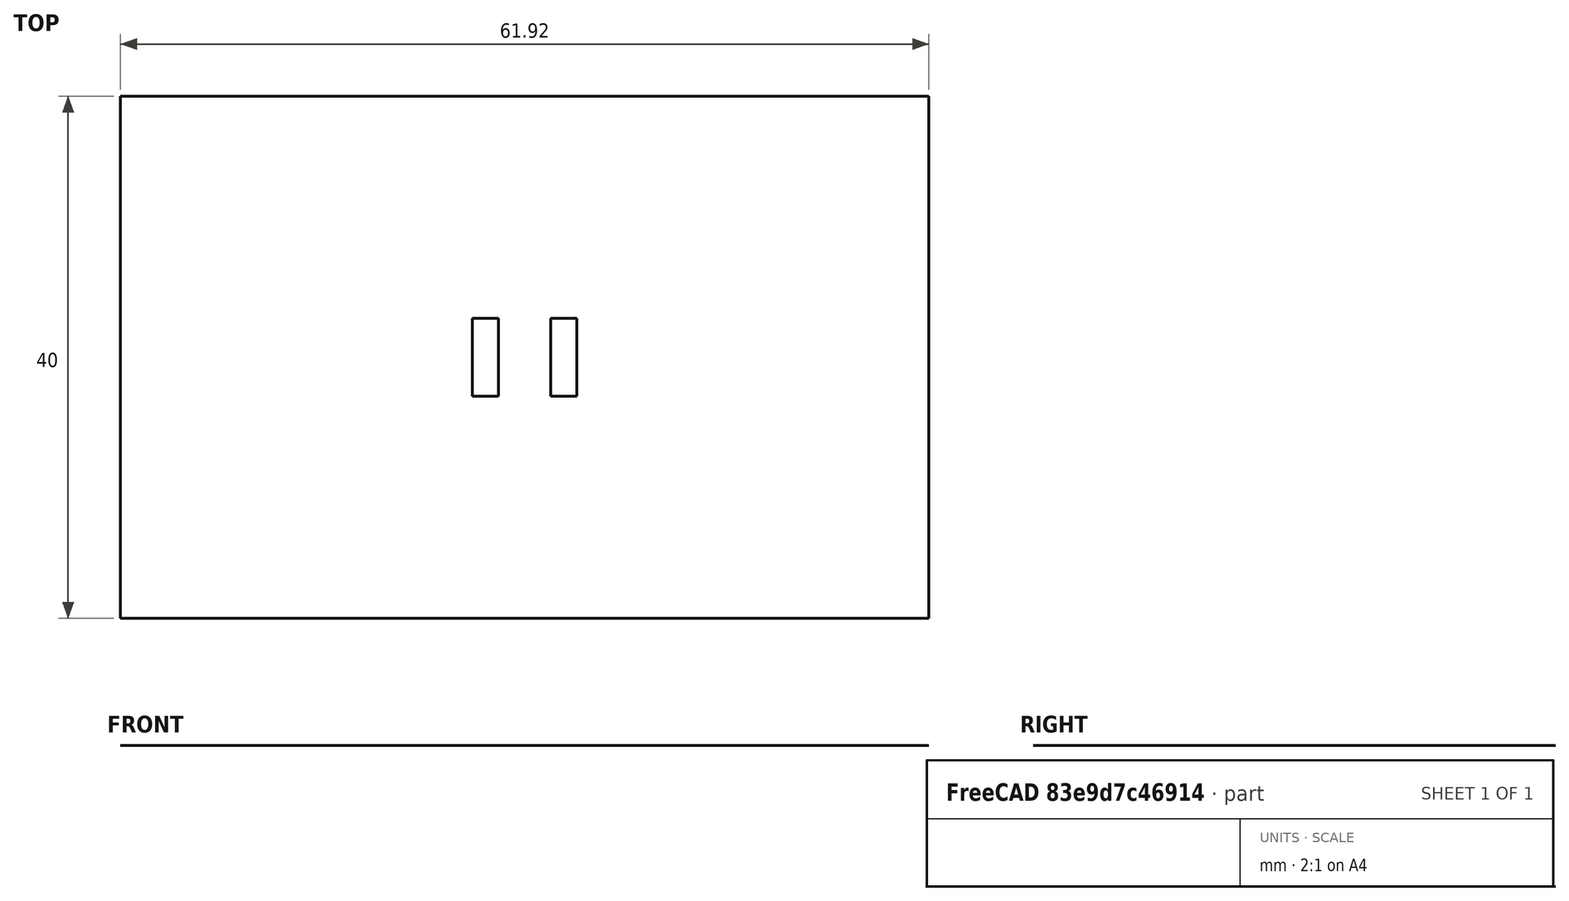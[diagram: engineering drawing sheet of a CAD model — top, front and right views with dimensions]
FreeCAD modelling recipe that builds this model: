
FCSTD DOCUMENT  (FreeCAD 1.0R39109 (Git))
Label: Magnetics-2D
License: All rights reserved
LicenseURL: https://en.wikipedia.org/wiki/All_rights_reserved
objects: Part::RuledSurface×2, App::MaterialObjectPython×2, Fem::ConstraintPython×2, Sketcher::SketchObject×1, Part::Face×1, Part::FeaturePython×1, App::FeaturePython×1, Fem::FemMeshShapeBaseObjectPython×1, App::TextDocument×1, Fem::FemPostContoursFilter×1, Fem::FemPostDataAlongLineFilter×1, Fem::FemPostPipeline×1, Fem::FemSolverObjectPython×1, Fem::FemAnalysis×1
note: 6 computed .brp shape members not serialized (recipe doc carries the construction recipe); baked Part::Feature solids carry a one-line shape summary decoded from their .brp

FEATURE [Sketcher::SketchObject] Sketch
  ArcFitTolerance = 1e-06
  FullyConstrained = true
  MakeInternals = false
  sketch-geometry (12):
    g0: LineSegment StartX=-30.9563 StartY=20 StartZ=0 EndX=-30.9563 EndY=-20 EndZ=0
    g1: LineSegment StartX=-30.9563 StartY=-20 StartZ=0 EndX=30.9563 EndY=-20 EndZ=0
    g2: LineSegment StartX=30.9563 StartY=-20 StartZ=0 EndX=30.9563 EndY=20 EndZ=0
    g3: LineSegment StartX=30.9563 StartY=20 StartZ=0 EndX=-30.9563 EndY=20 EndZ=0
    g4: LineSegment StartX=-4 StartY=3 StartZ=0 EndX=-4 EndY=-3 EndZ=0
    g5: LineSegment StartX=-4 StartY=-3 StartZ=0 EndX=-2 EndY=-3 EndZ=0
    g6: LineSegment StartX=-2 StartY=-3 StartZ=0 EndX=-2 EndY=3 EndZ=0
    g7: LineSegment StartX=-2 StartY=3 StartZ=0 EndX=-4 EndY=3 EndZ=0
    g8: LineSegment StartX=2 StartY=3 StartZ=0 EndX=2 EndY=-3 EndZ=0
    g9: LineSegment StartX=2 StartY=-3 StartZ=0 EndX=4 EndY=-3 EndZ=0
    g10: LineSegment StartX=4 StartY=-3 StartZ=0 EndX=4 EndY=3 EndZ=0
    g11: LineSegment StartX=4 StartY=3 StartZ=0 EndX=2 EndY=3 EndZ=0
  constraints (31):
    c: Coincident(g0,g1)
    c: Coincident(g1,g2)
    c: Coincident(g2,g3)
    c: Coincident(g3,g0)
    c: Vertical(g2)
    c: Horizontal(g1)
    c: Coincident(g4,g5)
    c: Coincident(g5,g6)
    c: Coincident(g6,g7)
    c: Coincident(g7,g4)
    c: Vertical(g6)
    c: Horizontal(g5)
    c: Horizontal(g7)
    c: Coincident(g8,g9)
    c: Coincident(g9,g10)
    c: Coincident(g10,g11)
    c: Coincident(g11,g8)
    c: Vertical(g8)
    c: Horizontal(g9)
    c: Horizontal(g11)
    c: Symmetric(g0,g2,g-2)
    c: Symmetric(g0,g0,g-1)
    c: Symmetric(g4,g4,g-1)
    c: Symmetric(g6,g8,g-2)
    c: Symmetric(g10,g9,g-1)
    c: Equal(g9,g5)
    c: Equal(g6,g8)
    c: DistanceX(g11,g11) = 2
    c: DistanceY(g10,g10) = 6
    c: DistanceX(g-1,g8) = 2
    c: DistanceY(g2,g2) = 40
FEATURE [Part::Face] Face
  FaceMakerClass = Part::FaceMakerBullseye
  Sources = -> [Sketch]
FEATURE [Part::RuledSurface] Ruled_Surface
  Curve1 = -> Sketch [Edge5]
  Curve2 = -> Sketch [Edge7]
  Orientation = 0
FEATURE [Part::RuledSurface] Ruled_Surface001
  Curve1 = -> Sketch [Edge9]
  Curve2 = -> Sketch [Edge11]
  Orientation = 0
FEATURE [Part::FeaturePython] BooleanFragments  # WARN: FeaturePython — macro-defined, semantics opaque (R4)
  Mode = 0
  Objects = -> [Face,Ruled_Surface,Ruled_Surface001]
  Tolerance = 0
FEATURE [App::FeaturePython] Magnetodynamic2D  # WARN: FeaturePython — macro-defined, semantics opaque (R4)
  AngularFrequency = 0
  BiCGstablDegree = 2
  CalculateCurrentDensity = false
  CalculateElectricField = false
  CalculateElementalFields = false
  CalculateHarmonicLoss = false
  CalculateJouleHeating = false
  CalculateMagneticFieldStrength = true
  CalculateMaxwellStress = false
  CalculateNodalFields = true
  CalculateNodalForces = true
  CalculateNodalHeating = false
  IdrsParameter = 2
  IsHarmonic = false
  LinearDirectMethod = 0
  LinearIterations = 500
  LinearIterativeMethod = 0
  LinearPreconditioning = 2
  LinearSolverType = 1
  LinearSystemSolverDisabled = false
  LinearTolerance = 1e-10
  NonlinearIterations = 20
  NonlinearNewtonAfterIterations = 3
  NonlinearNewtonAfterTolerance = 0.001
  NonlinearTolerance = 1e-07
  Priority = 10
  RelaxationFactor = 1
  Stabilize = true
  SteadyStateTolerance = 1e-05
  expr: LinearTolerance = 1e-10
  expr: NonlinearNewtonAfterTolerance = 0.001
  expr: NonlinearTolerance = 1e-07
  expr: SteadyStateTolerance = 1e-05
FEATURE [App::MaterialObjectPython] MaterialFluid  # material (typed FeaturePython)
  Category = 1
  Material = AuthorAndLicense=GPL-2.0-or-later; CardName=Air; Density=1.204e-09 kg/mm^3; Description=Dry air properties at 20 Degrees Celsius and 1 atm; DynamicViscosity=1.8e-08 kg/(mm*s); ElectricalConductivity=1e-21 s^3*A^2/(mm^3*kg); Father=Gas; KinematicViscosity=15.11 mm^2/s; License=GPL-2.0-or-later; Name=Air; PrandtlNumber=0.7; RelativePermeability=1; RelativePermittivity=1.00059; SpecificHeat=1.01e+09 mm^2/(s^2*K); ThermalConductivity=25.87 mm*kg/(s^3*K); ThermalExpansionCoefficient=0.00343 1/K
  References = -> [BooleanFragments]
  UUID = 94370b96-c97e-4a3f-83b2-11d7461f7da7
FEATURE [App::MaterialObjectPython] MaterialSolid  # material (typed FeaturePython)
  Category = 0
  Material = AmbientColor=(0.0020, 0.0020, 0.0020, 1.0); Author=Uwe Stöhr; CardName=Iron-Generic; Density=7.874e-06 kg/mm^3; DiffuseColor=(0.0000, 0.0000, 0.0000, 1.0); ElectricalConductivity=0.0103 s^3*A^2/(mm^3*kg); EmissiveColor=(0.0000, 0.0000, 0.0000, 1.0); Father=Metal; KindOfMaterial=Iron; Name=Iron-Generic; PoissonRatio=0.29; RelativePermeability=5000; ShearModulus=8.2e+07 kg/(mm*s^2); Shininess=0.06; SpecificHeat=4.605e+08 mm^2/(s^2*K); SpecularColor=(0.9800, 0.9800, 0.9800, 1.0); ThermalConductivity=80400 mm*kg/(s^3*K); ThermalExpansionCoefficient=1.18e-05 1/K; Transparency=0; UltimateTensileStrength=497000 kg/(mm*s^2); YieldStrength=428000 kg/(mm*s^2); YoungsModulus=2.11e+08 kg/(mm*s^2)
  References = -> [BooleanFragments]
  UUID = 1826c364-d26a-43fb-8f61-288281236836
FEATURE [Fem::ConstraintPython] ConstraintMagnetization  label="Magnetization-Left"  # FEM object (typed FeaturePython)
  Magnetization_im_1 = 0
  Magnetization_im_1_Disabled = true
  Magnetization_im_2 = 0
  Magnetization_im_2_Disabled = true
  Magnetization_im_3 = 0
  Magnetization_im_3_Disabled = true
  Magnetization_re_1 = 0
  Magnetization_re_1_Disabled = true
  Magnetization_re_2 = 5
  Magnetization_re_2_Disabled = false
  Magnetization_re_3 = 0
  Magnetization_re_3_Disabled = true
  NormalDirection = (0,0,1)
  Normals = (9) [(0,0,1),(0,0,1),(0,0,1),(0,0,1),(0,0,1),(0,0,1),(0,0,1),(0,0,1),(0,0,1)]
  Points = (9) [(-4,3,0),(-4,0,0),(-4,-3,0),(-3,3,0),(-3,0,0),(-3,-3,0),(-2,3,0),(-2,0,0),(-2,-3,0)]
  References = -> [BooleanFragments]
  Suppressed = false
FEATURE [Fem::ConstraintPython] ConstraintMagnetization001  label="Magnetization-Right"  # FEM object (typed FeaturePython)
  Magnetization_im_1 = 0
  Magnetization_im_1_Disabled = true
  Magnetization_im_2 = 0
  Magnetization_im_2_Disabled = true
  Magnetization_im_3 = 0
  Magnetization_im_3_Disabled = true
  Magnetization_re_1 = 0
  Magnetization_re_1_Disabled = true
  Magnetization_re_2 = -5
  Magnetization_re_2_Disabled = false
  Magnetization_re_3 = 0
  Magnetization_re_3_Disabled = true
  NormalDirection = (0,0,1)
  Normals = (9) [(0,0,1),(0,0,1),(0,0,1),(0,0,1),(0,0,1),(0,0,1),(0,0,1),(0,0,1),(0,0,1)]
  Points = (9) [(2,3,0),(2,0,0),(2,-3,0),(3,3,0),(3,0,0),(3,-3,0),(4,3,0),(4,0,0),(4,-3,0)]
  References = -> [BooleanFragments]
  Suppressed = false
FEATURE [Fem::FemMeshShapeBaseObjectPython] FEMMeshGmsh  # FEM object (typed FeaturePython)
  Algorithm2D = 0
  Algorithm3D = 0
  CharacteristicLengthMax = 0.5
  CharacteristicLengthMin = 0.1
  CoherenceMesh = true
  ElementDimension = 0
  ElementOrder = 1
  GeometryTolerance = 1e-06
  GroupsOfNodes = false
  HighOrderOptimize = 0
  MeshSizeFromCurvature = 12
  OptimizeNetgen = false
  OptimizeStd = true
  RecombinationAlgorithm = 0
  Recombine3DAll = false
  RecombineAll = false
  SecondOrderLinear = false
  Shape = -> BooleanFragments
  SubdivisionAlgorithm = 0
FEATURE [App::TextDocument] SolverElmerOutput
  Text = <blob: 22425 chars omitted>
FEATURE [Fem::FemPostContoursFilter] Contours
  Field = 2
  NoColor = false
  NumberOfContours = 10
  VectorMode = 0
FEATURE [Fem::FemPostDataAlongLineFilter] DataAlongLine
  PlotData = magnetic field strength
  PlotDataComponent = 0
  Point1 = (-18,0,0)
  Point2 = (18,0,0)
  Resolution = 100
  XAxisData = [0,0.36,0.719999,1.08,1.44,1.8,2.16,2.52,2.88,3.24,3.6,3.96,4.32,4.68,5.04,5.39999,5.76,6.11999,6.47999,6.83999,7.19999,7.55999,7.91999,8.27999,8.63999,8.99999,9.35999,9.71999,10.08,10.44,10.8,11.16,11.52,11.88,12.24,12.6,12.96,13.32,13.68,+62 more]
  YAxisData = [78.8099,84.7105,91.2889,98.2834,106.011,114.294,123.49,133.424,144.607,156.775,170.003,184.822,201.291,219.226,240.012,262.377,288.19,316.788,348.722,385.676,427.449,473.871,529.495,591.506,663.479,746.773,843.723,959.184,1092.9,1250.86,+71 more]
FEATURE [Fem::FemPostPipeline] SolverElmerResult
  Filter = -> [Contours,DataAlongLine]
  Mode = 2
FEATURE [Fem::FemSolverObjectPython] SolverElmer  # FEM object (typed FeaturePython)
  BDFOrder = 2
  CoordinateSystem = 0
  ElmerOutput = -> SolverElmerOutput
  ElmerResult = -> SolverElmerResult
  Group = -> [Magnetodynamic2D]
  OutputIntervals = [1]
  SimulationType = 1
  SteadyStateMaxIterations = 1
  SteadyStateMinIterations = 0
  TimestepIntervals = [100]
  TimestepSizes = [0.1]
FEATURE [Fem::FemAnalysis] Analysis
  Group = -> [SolverElmer,MaterialFluid,MaterialSolid,ConstraintMagnetization,ConstraintMagnetization001,FEMMeshGmsh,SolverElmerOutput,SolverElmerResult]
